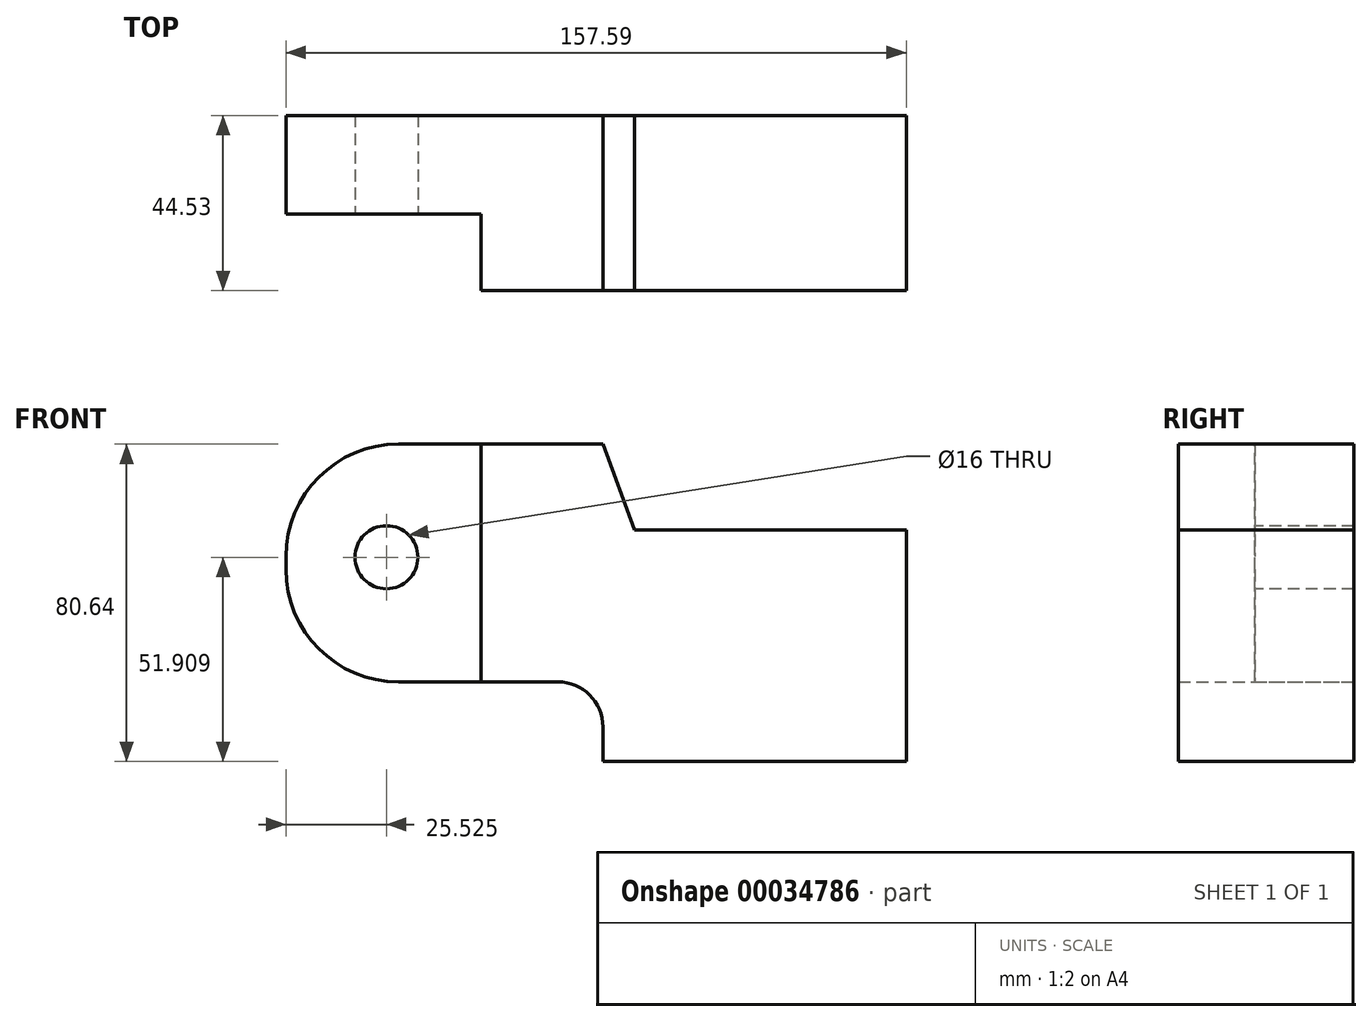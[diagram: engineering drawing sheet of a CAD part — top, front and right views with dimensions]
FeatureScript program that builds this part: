
annotation { "Feature Type Name" : "Feature", "Feature Type Description" : "" }
export const myFeature = defineFeature(function(context is Context, id is Id, definition is map)
    precondition{}
    {
        {
            var Q0;
            Q0=qCreatedBy(makeId("Front.planeOp"),FACE);
            var sketch = newSketch(context, id + "F0", { "sketchPlane" : qUnion([Q0])});
            skLineSegment(sketch, "E0.bottom", {"start": v(-80.5, 80.64) * mm, "end": v(0, 80.64) * mm});
            skLineSegment(sketch, "E0.top", {"start": v(0, 0) * mm, "end": v(77.09, 0) * mm});
            skLineSegment(sketch, "E0.left", {"start": v(-80.5, 80.64) * mm, "end": v(-80.5, 20.25) * mm});
            skLineSegment(sketch, "E1", {"start": v(-81.05, 20.25) * mm, "end": v(-11.43, 20.25) * mm});
            skLineSegment(sketch, "E2", {"start": v(0, 20.25) * mm, "end": v(0, 0) * mm});
            skLineSegment(sketch, "E3", {"start": v(0, 0) * mm, "end": v(0, 8.82) * mm});
            skPoint(sketch, "E4.visualSharp", {"position": v(0, 20.25) * mm});
            skArc(sketch, "E4.filletArc", {"start": v(0, 8.82) * mm, "mid": v(-3.35, 16.9) * mm, "end": v(-11.43, 20.25) * mm});
            skLineSegment(sketch, "E5", {"start": v(0, 80.64) * mm, "end": v(8.04, 58.78) * mm});
            skLineSegment(sketch, "E6", {"start": v(8.04, 58.78) * mm, "end": v(77.09, 58.78) * mm});
            skLineSegment(sketch, "E7", {"start": v(77.09, 58.78) * mm, "end": v(77.09, 0) * mm});
            skSolve(sketch);
        }
        {
            var Q0;
            Q0=makeQuery(id+"F0.imprint","IMPRINT",FACE,{"disambiguationData":[TD([[makeQuery(id+"F0.imprint","IMPRINT",EDGE,{"derivedFrom":sQuery(id+"F0.wireOp",EDGE,"E0.bottom")}),-1.0]])]});
            extrude(context, id + "F1", {"entities" : qUnion([Q0]), "depth" : 44.53 * mm});
        }
        {
            var Q0;
            Q0=makeQuery(id+"F1.opExtrude","SWEPT_FACE",FACE,{"disambiguationData":[OSD([sQuery(id+"F0.wireOp",EDGE,"E0.bottom")])]});
            var sketch = newSketch(context, id + "F2", { "sketchPlane" : qUnion([Q0])});
            skLineSegment(sketch, "E8.bottom", {"start": v(-80.5, -44.53) * mm, "end": v(-30.9, -44.53) * mm});
            skLineSegment(sketch, "E8.top", {"start": v(-80.5, -25.12) * mm, "end": v(-30.9, -25.12) * mm});
            skLineSegment(sketch, "E8.left", {"start": v(-80.5, -44.53) * mm, "end": v(-80.5, -25.12) * mm});
            skLineSegment(sketch, "E8.right", {"start": v(-30.9, -44.53) * mm, "end": v(-30.9, -25.12) * mm});
            skSolve(sketch);
        }
        {
            var Q0;
            Q0=makeQuery(id+"F2.imprint","IMPRINT",FACE,{"disambiguationData":[TD([[makeQuery(id+"F2.imprint","IMPRINT",EDGE,{"derivedFrom":sQuery(id+"F2.wireOp",EDGE,"E8.bottom")}),1.0]])]});
            extrude(context, id + "F3", {"entities" : qUnion([Q0]), "operationType" : NewBodyOperationType.REMOVE, "oppositeDirection" : true, "depth" : 66.47 * mm});
        }
        {
            var Q0;
            Q0=makeQuery(id+"F1.opExtrude","SWEPT_EDGE",EDGE,{"disambiguationData":[OSD([sQuery(id+"F0.wireOp",EDGE,"E0.bottom"),sQuery(id+"F0.wireOp",EDGE,"E0.left")])]});
            var Q1;
            Q1=makeQuery(id+"F1.opExtrude","SWEPT_EDGE",EDGE,{"disambiguationData":[OSD([sQuery(id+"F0.wireOp",EDGE,"E0.left"),sQuery(id+"F0.wireOp",EDGE,"E1")])]});
            fillet(context, id + "F4", {"entities" : qUnion([Q0, Q1]), "radius" : 28.55 * mm, "tangentPropagation" : true, "allowEdgeOverflow" : false});
        }
        {
            var Q0;
            Q0=makeQuery(id+"F3.boolean.opBoolean","COPY",FACE,{"derivedFrom":makeQuery(id+"F3.opExtrude","SWEPT_FACE",FACE,{"disambiguationData":[OSD([sQuery(id+"F2.wireOp",EDGE,"E8.top")])]})});
            var sketch = newSketch(context, id + "F5", { "sketchPlane" : qUnion([Q0])});
            skCircle(sketch, "E9", {"center": v(-54.98, 51.9) * mm, "radius": 8 * mm});
            skSolve(sketch);
        }
        {
            var Q0;
            Q0=makeQuery(id+"F5.imprint","IMPRINT",FACE,{"disambiguationData":[TD([[makeQuery(id+"F5.imprint","IMPRINT",EDGE,{"derivedFrom":sQuery(id+"F5.wireOp",EDGE,"E9")}),1.0]])]});
            extrude(context, id + "F6", {"entities" : qUnion([Q0]), "operationType" : NewBodyOperationType.REMOVE, "oppositeDirection" : true, "depth" : 25.4 * mm});
        }
    });
